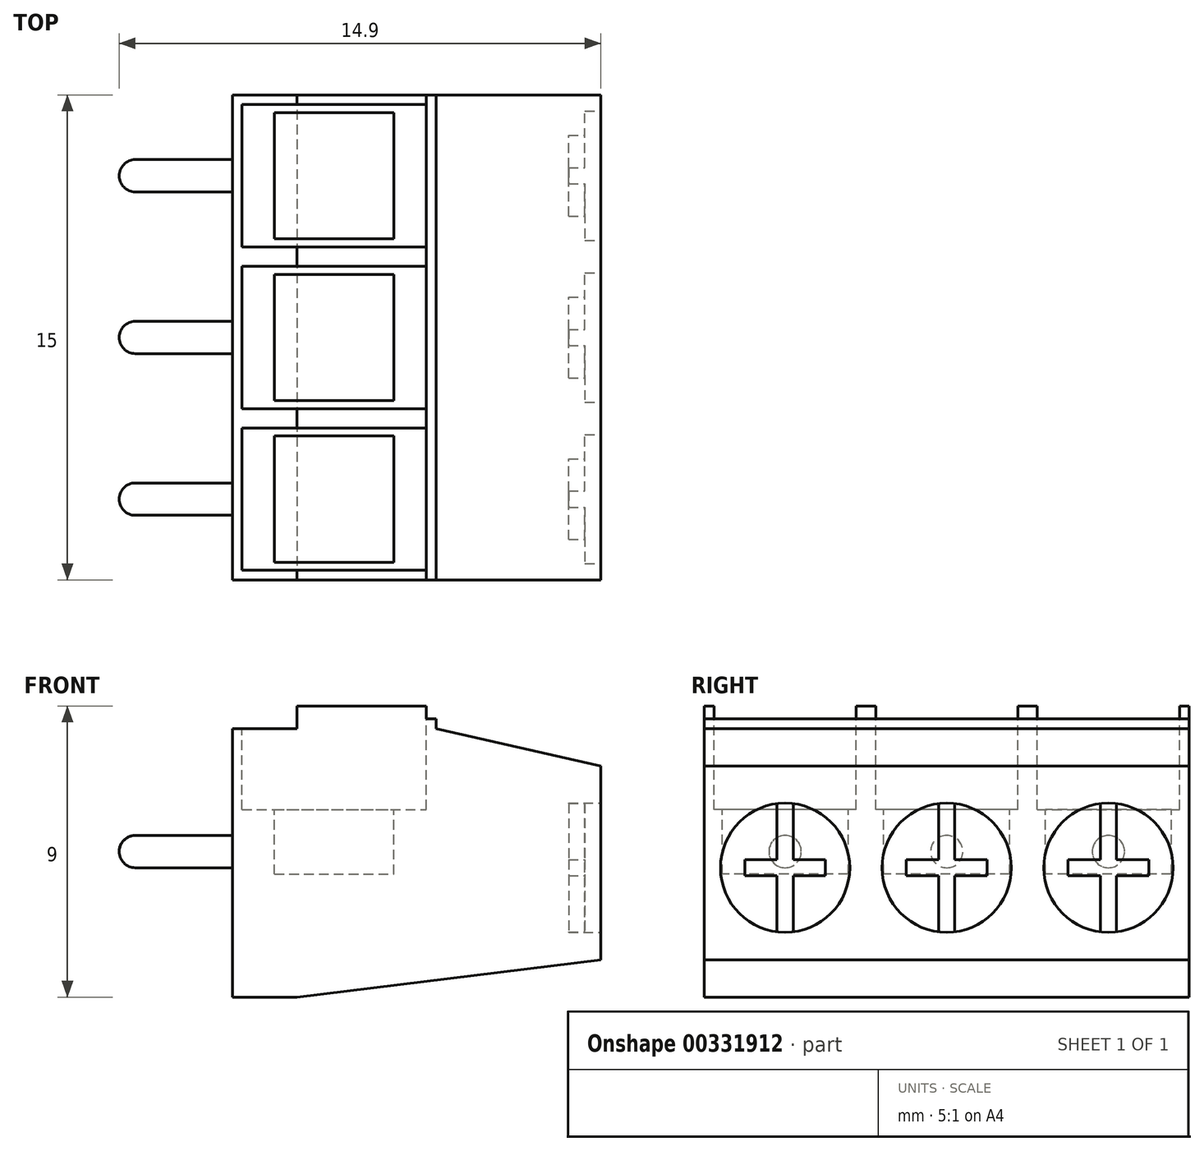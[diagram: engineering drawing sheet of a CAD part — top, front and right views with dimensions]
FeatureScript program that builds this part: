
annotation { "Feature Type Name" : "Feature", "Feature Type Description" : "" }
export const myFeature = defineFeature(function(context is Context, id is Id, definition is map)
    precondition{}
    {
        {
            var Q0;
            Q0=qCreatedBy(makeId("Top.planeOp"),FACE);
            var sketch = newSketch(context, id + "F0", { "sketchPlane" : qUnion([Q0])});
            skLineSegment(sketch, "E0.bottom", {"start": v(5.7, 7.5) * mm, "end": v(-5.7, 7.5) * mm});
            skLineSegment(sketch, "E0.top", {"start": v(5.7, -7.5) * mm, "end": v(-5.7, -7.5) * mm});
            skLineSegment(sketch, "E0.left", {"start": v(5.7, 7.5) * mm, "end": v(5.7, -7.5) * mm});
            skLineSegment(sketch, "E0.right", {"start": v(-5.7, 7.5) * mm, "end": v(-5.7, -7.5) * mm});
            skPoint(sketch, "E0.middle", {"position": v(0, 0) * mm});
            skSolve(sketch);
        }
        {
            var Q0;
            Q0 = qSketchRegion(id + "F0", true);
            extrude(context, id + "F1", {"entities" : qUnion([Q0]), "depth" : 8.3 * mm});
        }
        {
            var Q0;
            Q0=makeQuery(id+"F1.opExtrude","SWEPT_FACE",FACE,{"disambiguationData":[OSD([sQuery(id+"F0.wireOp",EDGE,"E0.top")])]});
            var sketch = newSketch(context, id + "F2", { "sketchPlane" : qUnion([Q0])});
            skLineSegment(sketch, "E1", {"start": v(-3.7, 0) * mm, "end": v(5.7, 1.15) * mm});
            skLineSegment(sketch, "E2", {"start": v(5.7, 7.15) * mm, "end": v(0.6, 8.3) * mm});
            skLineSegment(sketch, "E3", {"start": v(5.7, 1.15) * mm, "end": v(5.7, 0) * mm});
            skLineSegment(sketch, "E4", {"start": v(5.7, 0) * mm, "end": v(-3.7, 0) * mm});
            skLineSegment(sketch, "E5", {"start": v(0.6, 8.3) * mm, "end": v(5.7, 8.3) * mm});
            skLineSegment(sketch, "E6", {"start": v(5.7, 8.3) * mm, "end": v(5.7, 7.15) * mm});
            skSolve(sketch);
        }
        {
            var Q0;
            Q0 = qSketchRegion(id + "F2", true);
            extrude(context, id + "F3", {"entities" : qUnion([Q0]), "operationType" : NewBodyOperationType.REMOVE, "endBound" : BoundingType.THROUGH_ALL, "oppositeDirection" : true, "depth" : 25 * mm});
        }
        {
            var Q0;
            Q0=makeQuery(id+"F1.opExtrude","SWEPT_FACE",FACE,{"disambiguationData":[OSD([sQuery(id+"F0.wireOp",EDGE,"E0.top")])]});
            var sketch = newSketch(context, id + "F4", { "sketchPlane" : qUnion([Q0])});
            skLineSegment(sketch, "E7", {"start": v(-3.7, 8.3) * mm, "end": v(-3.7, 9) * mm});
            skLineSegment(sketch, "E8", {"start": v(-3.7, 9) * mm, "end": v(0.3, 9) * mm});
            skLineSegment(sketch, "E9", {"start": v(0.6, 8.3) * mm, "end": v(0.6, 8.6) * mm});
            skLineSegment(sketch, "E10", {"start": v(0.6, 8.6) * mm, "end": v(0.3, 8.6) * mm});
            skLineSegment(sketch, "E11", {"start": v(0.3, 8.6) * mm, "end": v(0.3, 9) * mm});
            skLineSegment(sketch, "E12", {"start": v(-3.7, 8.3) * mm, "end": v(0.6, 8.3) * mm});
            skSolve(sketch);
        }
        {
            var Q0;
            Q0 = qSketchRegion(id + "F4", true);
            var Q1;
            Q1=makeQuery(id+"F1.opExtrude","SWEPT_FACE",FACE,{"disambiguationData":[OSD([sQuery(id+"F0.wireOp",EDGE,"E0.bottom")])]});
            extrude(context, id + "F5", {"entities" : qUnion([Q0]), "operationType" : NewBodyOperationType.ADD, "endBound" : BoundingType.UP_TO_SURFACE, "oppositeDirection" : true, "endBoundEntityFace" : qUnion([Q1]), "depth" : 25 * mm});
        }
        {
            var Q0;
            Q0=makeQuery(id+"F5.opExtrude","SWEPT_FACE",FACE,{"disambiguationData":[OSD([sQuery(id+"F4.wireOp",EDGE,"E8")])]});
            var sketch = newSketch(context, id + "F6", { "sketchPlane" : qUnion([Q0])});
            skLineSegment(sketch, "E13.bottom", {"start": v(-5.4, 2.2) * mm, "end": v(0.3, 2.2) * mm});
            skLineSegment(sketch, "E13.top", {"start": v(-5.4, -2.2) * mm, "end": v(0.3, -2.2) * mm});
            skLineSegment(sketch, "E13.left", {"start": v(-5.4, 2.2) * mm, "end": v(-5.4, -2.2) * mm});
            skLineSegment(sketch, "E13.right", {"start": v(0.3, 2.2) * mm, "end": v(0.3, -2.2) * mm});
            skLineSegment(sketch, "E14", {"start": v(5.75, 0) * mm, "end": v(-7.65, 0) * mm, "construction": true});
            skLineSegment(sketch, "E15.0.1.0", {"start": v(-5.4, 7.2) * mm, "end": v(0.3, 7.2) * mm});
            skLineSegment(sketch, "E15.0.1.1", {"start": v(-5.4, 2.8) * mm, "end": v(0.3, 2.8) * mm});
            skLineSegment(sketch, "E15.0.1.2", {"start": v(0.3, 7.2) * mm, "end": v(0.3, 2.8) * mm});
            skLineSegment(sketch, "E15.direction2", {"start": v(-5.4, 2.8) * mm, "end": v(-5.4, 7.2) * mm});
            skLineSegment(sketch, "E16.MirrorCS", {"start": v(-5.4, -2.8) * mm, "end": v(0.3, -2.8) * mm});
            skLineSegment(sketch, "E17.MirrorCS", {"start": v(-5.4, -2.8) * mm, "end": v(-5.4, -7.2) * mm});
            skLineSegment(sketch, "E18.MirrorCS", {"start": v(-5.4, -7.2) * mm, "end": v(0.3, -7.2) * mm});
            skLineSegment(sketch, "E19.MirrorCS", {"start": v(0.3, -7.2) * mm, "end": v(0.3, -2.8) * mm});
            skSolve(sketch);
        }
        {
            var Q0;
            Q0 = qSketchRegion(id + "F6", true);
            extrude(context, id + "F7", {"entities" : qUnion([Q0]), "operationType" : NewBodyOperationType.REMOVE, "oppositeDirection" : true, "depth" : 3.2 * mm});
        }
        {
            var Q0;
            Q0=makeQuery(id+"F1.opExtrude","SWEPT_FACE",FACE,{"disambiguationData":[OSD([sQuery(id+"F0.wireOp",EDGE,"E0.right")])]});
            var sketch = newSketch(context, id + "F8", { "sketchPlane" : qUnion([Q0])});
            skCircle(sketch, "E20", {"center": v(0, 4.5) * mm, "radius": 0.5 * mm});
            skCircle(sketch, "E21", {"center": v(5, 4.5) * mm, "radius": 0.5 * mm});
            skCircle(sketch, "E22", {"center": v(-5, 4.5) * mm, "radius": 0.5 * mm});
            skSolve(sketch);
        }
        {
            var Q0;
            Q0 = qSketchRegion(id + "F8", true);
            extrude(context, id + "F9", {"entities" : qUnion([Q0]), "operationType" : NewBodyOperationType.ADD, "depth" : 3.5 * mm});
        }
        {
            var Q0;
            Q0=makeQuery(id+"F1.opExtrude","SWEPT_FACE",FACE,{"disambiguationData":[OSD([sQuery(id+"F0.wireOp",EDGE,"E0.left")])]});
            var sketch = newSketch(context, id + "F10", { "sketchPlane" : qUnion([Q0])});
            skCircle(sketch, "E23", {"center": v(0, 4) * mm, "radius": 2 * mm});
            skCircle(sketch, "E24", {"center": v(5, 4) * mm, "radius": 2 * mm});
            skCircle(sketch, "E25", {"center": v(-5, 4) * mm, "radius": 2 * mm});
            skSolve(sketch);
        }
        {
            var Q0;
            Q0 = qSketchRegion(id + "F10", true);
            extrude(context, id + "F11", {"entities" : qUnion([Q0]), "operationType" : NewBodyOperationType.REMOVE, "oppositeDirection" : true, "depth" : 0.5 * mm});
        }
        {
            var Q0;
            Q0=makeQuery(id+"F1.opExtrude","SWEPT_FACE",FACE,{"disambiguationData":[OSD([sQuery(id+"F0.wireOp",EDGE,"E0.left")])]});
            var sketch = newSketch(context, id + "F12", { "sketchPlane" : qUnion([Q0])});
            skLineSegment(sketch, "E26.left", {"start": v(-5.25, 5.98) * mm, "end": v(-5.25, 4.25) * mm});
            skLineSegment(sketch, "E26.right", {"start": v(-4.75, 5.98) * mm, "end": v(-4.75, 4.25) * mm});
            skLineSegment(sketch, "E27.bottom", {"start": v(-6.25, 4.25) * mm, "end": v(-5.25, 4.25) * mm});
            skLineSegment(sketch, "E27.top", {"start": v(-6.25, 3.75) * mm, "end": v(-5.25, 3.75) * mm});
            skLineSegment(sketch, "E28", {"start": v(-5, 8.3) * mm, "end": v(-5, -1.7) * mm, "construction": true});
            skLineSegment(sketch, "E29", {"start": v(-8.7, 4) * mm, "end": v(-1.4, 4) * mm, "construction": true});
            skArc(sketch, "E30.trimOffspring", {"start": v(-4.75, 5.98) * mm, "mid": v(-5, 6) * mm, "end": v(-5.25, 5.98) * mm});
            skArc(sketch, "E31.trimOffspring", {"start": v(-5.25, 2.02) * mm, "mid": v(-5, 2) * mm, "end": v(-4.75, 2.02) * mm});
            skLineSegment(sketch, "E32", {"start": v(-6.25, 4.25) * mm, "end": v(-6.25, 3.75) * mm});
            skLineSegment(sketch, "E33", {"start": v(-3.75, 4.25) * mm, "end": v(-3.75, 3.75) * mm});
            skLineSegment(sketch, "E34.trimOffspring", {"start": v(-4.75, 3.75) * mm, "end": v(-4.75, 2.02) * mm});
            skLineSegment(sketch, "E35.trimOffspring", {"start": v(-5.25, 3.75) * mm, "end": v(-5.25, 2.02) * mm});
            skLineSegment(sketch, "E36.trimOffspring", {"start": v(-4.75, 3.75) * mm, "end": v(-3.75, 3.75) * mm});
            skLineSegment(sketch, "E37.trimOffspring", {"start": v(-4.75, 4.25) * mm, "end": v(-3.75, 4.25) * mm});
            skLineSegment(sketch, "E38.1.0.0", {"start": v(0.25, 5.98) * mm, "end": v(0.25, 4.25) * mm});
            skArc(sketch, "E38.1.0.1", {"start": v(0.25, 5.98) * mm, "mid": v(0, 6) * mm, "end": v(-0.25, 5.98) * mm});
            skLineSegment(sketch, "E38.1.0.2", {"start": v(-0.25, 5.98) * mm, "end": v(-0.25, 4.25) * mm});
            skLineSegment(sketch, "E38.1.0.3", {"start": v(-1.25, 4.25) * mm, "end": v(-0.25, 4.25) * mm});
            skLineSegment(sketch, "E38.1.0.4", {"start": v(0.25, 4.25) * mm, "end": v(1.25, 4.25) * mm});
            skLineSegment(sketch, "E38.1.0.5", {"start": v(0.25, 3.75) * mm, "end": v(1.25, 3.75) * mm});
            skLineSegment(sketch, "E38.1.0.6", {"start": v(1.25, 4.25) * mm, "end": v(1.25, 3.75) * mm});
            skLineSegment(sketch, "E38.1.0.7", {"start": v(-1.25, 4.25) * mm, "end": v(-1.25, 3.75) * mm});
            skLineSegment(sketch, "E38.1.0.8", {"start": v(-1.25, 3.75) * mm, "end": v(-0.25, 3.75) * mm});
            skLineSegment(sketch, "E38.1.0.9", {"start": v(-0.25, 3.75) * mm, "end": v(-0.25, 2.02) * mm});
            skArc(sketch, "E38.1.0.10", {"start": v(-0.25, 2.02) * mm, "mid": v(0, 2) * mm, "end": v(0.25, 2.02) * mm});
            skLineSegment(sketch, "E38.2.0.0", {"start": v(5.25, 5.98) * mm, "end": v(5.25, 4.25) * mm});
            skArc(sketch, "E38.2.0.1", {"start": v(5.25, 5.98) * mm, "mid": v(5, 6) * mm, "end": v(4.75, 5.98) * mm});
            skLineSegment(sketch, "E38.2.0.2", {"start": v(4.75, 5.98) * mm, "end": v(4.75, 4.25) * mm});
            skLineSegment(sketch, "E38.2.0.3", {"start": v(3.75, 4.25) * mm, "end": v(4.75, 4.25) * mm});
            skLineSegment(sketch, "E38.2.0.4", {"start": v(5.25, 4.25) * mm, "end": v(6.25, 4.25) * mm});
            skLineSegment(sketch, "E38.2.0.5", {"start": v(5.25, 3.75) * mm, "end": v(6.25, 3.75) * mm});
            skLineSegment(sketch, "E38.2.0.6", {"start": v(6.25, 4.25) * mm, "end": v(6.25, 3.75) * mm});
            skLineSegment(sketch, "E38.2.0.7", {"start": v(3.75, 4.25) * mm, "end": v(3.75, 3.75) * mm});
            skLineSegment(sketch, "E38.2.0.8", {"start": v(3.75, 3.75) * mm, "end": v(4.75, 3.75) * mm});
            skLineSegment(sketch, "E38.2.0.9", {"start": v(4.75, 3.75) * mm, "end": v(4.75, 2.02) * mm});
            skArc(sketch, "E38.2.0.10", {"start": v(4.75, 2.02) * mm, "mid": v(5, 2) * mm, "end": v(5.25, 2.02) * mm});
            skLineSegment(sketch, "E38.direction1", {"start": v(-4.75, 4.25) * mm, "end": v(0.25, 4.25) * mm, "construction": true});
            skLineSegment(sketch, "E39", {"start": v(0.25, 3.75) * mm, "end": v(0.25, 2.02) * mm});
            skLineSegment(sketch, "E40", {"start": v(5.25, 3.75) * mm, "end": v(5.25, 2.02) * mm});
            skSolve(sketch);
        }
        {
            var Q0;
            Q0 = qSketchRegion(id + "F12", true);
            extrude(context, id + "F13", {"entities" : qUnion([Q0]), "operationType" : NewBodyOperationType.REMOVE, "oppositeDirection" : true, "depth" : 1 * mm});
        }
        {
            var Q0;
            Q0=makeQuery(id+"F9.opExtrude","CAP_FACE",FACE,{"disambiguationData":[OSD([sQuery(id+"F8.wireOp",EDGE,"E22")])],"isStart":false});
            var Q1;
            Q1=makeQuery(id+"F9.opExtrude","CAP_FACE",FACE,{"disambiguationData":[OSD([sQuery(id+"F8.wireOp",EDGE,"E20")])],"isStart":false});
            var Q2;
            Q2=makeQuery(id+"F9.opExtrude","CAP_FACE",FACE,{"disambiguationData":[OSD([sQuery(id+"F8.wireOp",EDGE,"E21")])],"isStart":false});
            fillet(context, id + "F14", {"entities" : qUnion([Q0, Q1, Q2]), "radius" : 0.5 * mm, "tangentPropagation" : true, "allowEdgeOverflow" : false});
        }
        {
            var Q0;
            Q0=makeQuery(id+"F7.boolean.opBoolean","COPY",FACE,{"derivedFrom":makeQuery(id+"F7.opExtrude","CAP_FACE",FACE,{"disambiguationData":[OSD([sQuery(id+"F6.wireOp",EDGE,"E13.bottom"),sQuery(id+"F6.wireOp",EDGE,"E13.top"),sQuery(id+"F6.wireOp",EDGE,"E13.left"),sQuery(id+"F6.wireOp",EDGE,"E13.right")])],"isStart":false})});
            var sketch = newSketch(context, id + "F15", { "sketchPlane" : qUnion([Q0])});
            skLineSegment(sketch, "E41.bottom", {"start": v(-4.4, 6.95) * mm, "end": v(-0.7, 6.95) * mm});
            skLineSegment(sketch, "E41.top", {"start": v(-4.4, 3.05) * mm, "end": v(-0.7, 3.05) * mm});
            skLineSegment(sketch, "E41.left", {"start": v(-4.4, 6.95) * mm, "end": v(-4.4, 3.05) * mm});
            skLineSegment(sketch, "E41.right", {"start": v(-0.7, 6.95) * mm, "end": v(-0.7, 3.05) * mm});
            skLineSegment(sketch, "E42", {"start": v(-2.55, 2.2) * mm, "end": v(-2.55, 12.24) * mm, "construction": true});
            skLineSegment(sketch, "E43", {"start": v(-5.4, 0) * mm, "end": v(8.63, 0) * mm, "construction": true});
            skPoint(sketch, "E43.endSnap0", {"position": v(-5.4, 0) * mm});
            skLineSegment(sketch, "E44", {"start": v(-5.47, 5) * mm, "end": v(2.68, 5) * mm, "construction": true});
            skPoint(sketch, "E45.orphan", {"position": v(0, 3.05) * mm});
            skLineSegment(sketch, "E46.0.1.0", {"start": v(-4.4, 1.95) * mm, "end": v(-4.4, -1.95) * mm});
            skLineSegment(sketch, "E46.0.1.1", {"start": v(-4.4, -1.95) * mm, "end": v(-0.7, -1.95) * mm});
            skLineSegment(sketch, "E46.0.1.2", {"start": v(-4.4, 1.95) * mm, "end": v(-0.7, 1.95) * mm});
            skLineSegment(sketch, "E46.0.1.3", {"start": v(-0.7, 1.95) * mm, "end": v(-0.7, -1.95) * mm});
            skLineSegment(sketch, "E46.0.2.0", {"start": v(-4.4, -3.05) * mm, "end": v(-4.4, -6.95) * mm});
            skLineSegment(sketch, "E46.0.2.1", {"start": v(-4.4, -6.95) * mm, "end": v(-0.7, -6.95) * mm});
            skLineSegment(sketch, "E46.0.2.2", {"start": v(-4.4, -3.05) * mm, "end": v(-0.7, -3.05) * mm});
            skLineSegment(sketch, "E46.0.2.3", {"start": v(-0.7, -3.05) * mm, "end": v(-0.7, -6.95) * mm});
            skLineSegment(sketch, "E46.direction1", {"start": v(-4.4, 3.05) * mm, "end": v(20.6, 3.05) * mm, "construction": true});
            skLineSegment(sketch, "E46.direction2", {"start": v(-4.4, 3.05) * mm, "end": v(-4.4, -1.95) * mm, "construction": true});
            skSolve(sketch);
        }
        {
            var Q0;
            Q0 = qSketchRegion(id + "F15", true);
            extrude(context, id + "F16", {"entities" : qUnion([Q0]), "operationType" : NewBodyOperationType.REMOVE, "oppositeDirection" : true, "depth" : 2 * mm});
        }
    });
